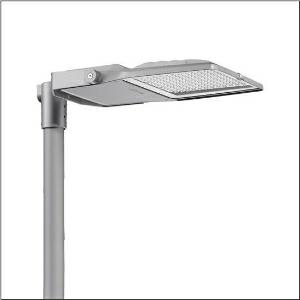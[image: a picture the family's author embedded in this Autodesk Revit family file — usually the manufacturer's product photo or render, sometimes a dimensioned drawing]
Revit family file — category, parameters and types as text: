
# Revit family: floodlight_fl_21_iq_midi___pl43_5xa7781e2a3a_1390
name_source: partatom
category: Lighting Fixtures
units: mm (PartAtom-declared; Revit-internal decimal feet)

## family parameters
Cut with Voids When Loaded = No
Host = Face
Light Source = No
Part Type = Normal
Room Calculation Point = No
Round Connector Dimension = Use Diameter
Shared = No

## types (1)
- --- (1 x LED, 27540 lm, 208.1 W, 3000K)
    Apparent Load = 208 VA
    CIE Flux Codes = 27 78 99 100 100
    Color Rendering = 70
    Color Temperature = 3000K
    Default Elevation = 1800 mm
    Description = Floodlight FL 21 iQ midi, floodlight, primary light control with lens, of PMMA, primary optical cover: protective disc, of toughened safety glass, transparent, light distribution: PL43, light emission: direct distribution, installation type: surface-mounted, lamps: LED, High Power LED, rated values: 27.540lm | 208,1W | 132,3lm/W (begin service life); end service life: 27.540lm | 227,1W; at 50% lumin. flux: 13.770lm | 90,1W | 152,8lm/W, colour temperature: 3000K, colour rendering: CRI > 70, light colour: 730, light setting 1 begin service life: 100% | 27.540lm | 208,1W | 132,3lm/W | 3.000K, light setting 1 end service life: 227,1W, further light settings possible, control: optimised constant luminous flux control (CLO 2.0), Desk-Remote (wireless, voltage-free reading and setting of iQ features in the workshop via application-optimized NFC function/RFID function), Light-Fading, Smart-Wire, Night-Set, Lumen-Switch, Temp-Guard, Auto-Match, pre-setting: linear dimming characteristic, with terminal, 6-pole, mains connection: 220..240V, AC, 50/60Hz, luminaire housing, of diecast aluminium, powder-coated, SITECO metallic grey (DB 702S), corrosivity category C5 mid according to DIN EN ISO 12944suitable for swimming poolschlorine-resistant, sealing non-destructively replaceable, please order mast flange separately, mast bracket, of steel, galvanised, powder-coated, SITECO metallic grey (DB 702S), protection rating (complete): IP66, insulation class (complete): insulation class II (safety insulation), certification: CE, ENEC, VDE, protection symbol: D, impact resistance: IK08, permissible operating ambient temperature: -40..+40°C, permissible operating ambient temperature for outdoor applications: -40..+50°C, standard: DIN EN 12944, LABS conformity tested according to VDMA 24364:2018-05, packaging unit: 1 piece

Light Distribution: PL43
    Height = 76 mm
    Lamp = 1 x LED
    Lamp Light Flux = 27540 lm
    Lamp Power = 208.1 W
    Lamp count = 1
    Length = 657 mm
    Luminous efficacy = 132 lm/W
    Manufacturer = Siteco
    ModVariant = No
    Model = 5XA7781E2A3A
    Number of Poles = 1
    OnlyDefault = Yes
    Power Factor = 1
    Product Name = Floodlight FL 21 iQ midi | PL43
    Product group = floodlight | pylon annexe
    ProductGroupID = 6201
    Protection Class = Protection class II
    Protection Degree = IP 66
    RLX_Detail_Level = 1
    RLX_Emergency_Light_Flux = 0 lm
    RLX_Emergency_Type = 0
    RLX_Emergency_Type_DB = No
    RlxData = <blob elided: 153957 chars, md5=cc42f74f>
    Socket = socket
    Standby Power = 0 W
    System Light Flux = 27540 lm
    System Power = 208 W
    Type Comments = factory setting: luminous flux: 100 % | dim-lin: 254 | 710 mA
    Type Image = l_1007123.jpg
    URL = http://relux.com
    VarID = @adj_105321
    Voltage = 0 V
    Weight = 0.00 kg
    Width = 442 mm

## geometry (parser evidence)
native form markers: Blend x4, Sweep x13
no freeform markers — native parametric forms only
